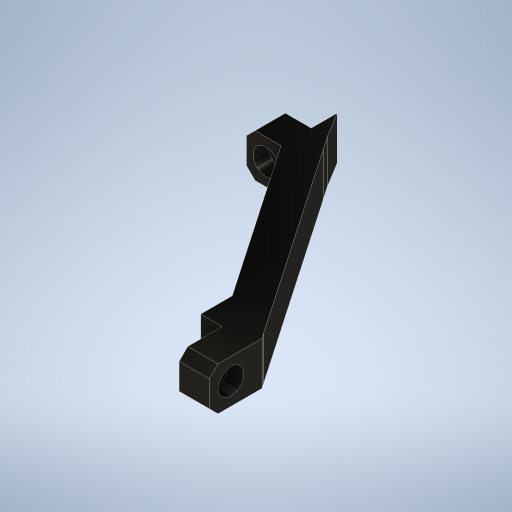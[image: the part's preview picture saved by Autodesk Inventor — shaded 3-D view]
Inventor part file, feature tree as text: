
AUTODESK INVENTOR PART (.ipt)
format: ipt  version: 2024.3 (Build 283343000, 343)  size: 316,928 bytes
history: native  units: mm
features: extrude x7, sketch x7, chamfer x1
ambient origin geometry x8: Origin, YZ Plane, XZ Plane, XY Plane, X Axis, Y Axis, Z Axis, Center Point
bodies: Solid1 (feature_tree)
feature tree (15):
  extrude  "Extrusion1"  Depth=7.0mm
  chamfer  "Chamfer1"  Distance=10.0mm
  extrude  "Extrusion2"  Depth=7.0mm
  extrude  "Extrusion3"  Depth=7.0mm
  extrude  "Extrusion4"  Depth=10.0mm
  extrude  "Extrusion5"  Depth=10.0mm
  extrude  "Extrusion6"  TaperAngle=135.0deg  [1 undecoded]
  extrude  "Extrusion7"  Depth=3.5mm
  sketch  "Sketch1"  dims[d0=10.0mm d1=7.0mm]
  sketch  "Sketch2"  dims[d7=29.5mm d12=10.0mm d13=0.0mm]
  sketch  "Sketch3"  dims[d14=50.1mm d15=7.0mm]
  sketch  "Sketch4"  dims[d16=8.0mm d17=7.0mm]
  sketch  "Sketch5"  dims[d18=2.0mm d19=2.0mm d20=45.0deg d21=10.0mm]
  sketch  "Sketch6"  dims[d22=10.0mm d23=3.2mm]
  sketch  "Sketch7"  dims[d24=0.0mm d25=0.0mm d26=135.0deg d27=3.5mm d28=3.0mm d29=10.0mm d30=0.0mm d31=6.0mm d32=3.5mm d33=0.0mm d34=6.0mm d35=3.5mm d36=0.0mm d37=5.0mm d38=90.0deg d39=10.0mm d40=0.0mm d41=3.662mm d42=6.0mm d43=10.0mm d44=0.0mm]
note: 1 required parameter value undecoded (feature->parameter linkage not recoverable at this tier; creation-order binding heuristic only, values carry confidence <= 0.55)
